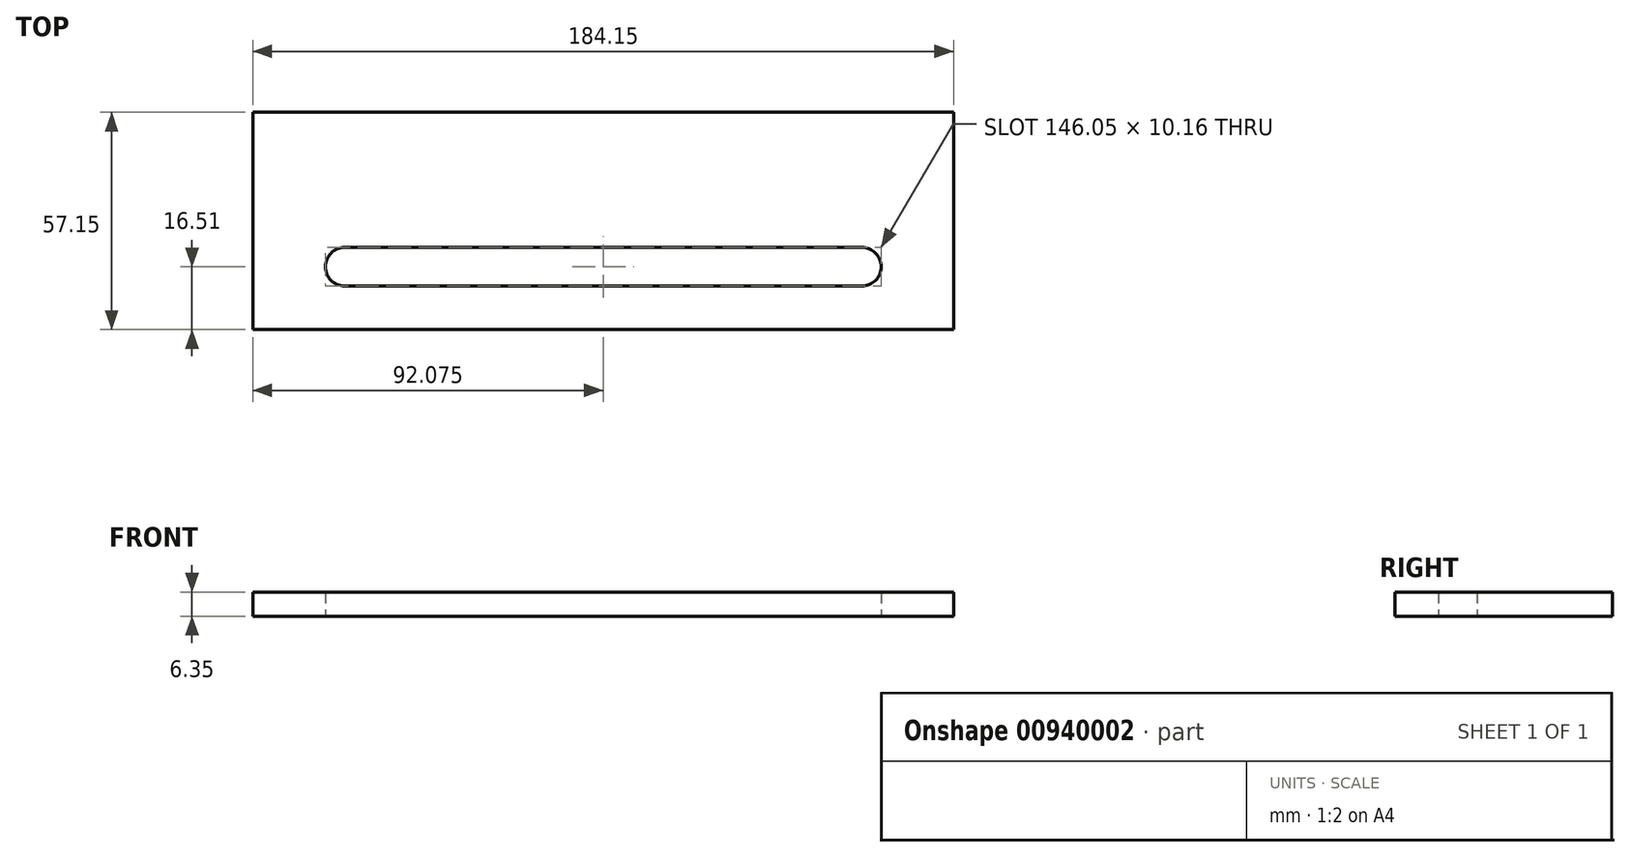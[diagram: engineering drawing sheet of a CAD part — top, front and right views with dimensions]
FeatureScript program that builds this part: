
annotation { "Feature Type Name" : "Feature", "Feature Type Description" : "" }
export const myFeature = defineFeature(function(context is Context, id is Id, definition is map)
    precondition{}
    {
        {
            var Q0;
            Q0=qCreatedBy(makeId("Top.planeOp"),FACE);
            var sketch = newSketch(context, id + "F0", { "sketchPlane" : qUnion([Q0])});
            skLineSegment(sketch, "E0.bottom", {"start": v(0, 0) * mm, "end": v(184.15, 0) * mm});
            skLineSegment(sketch, "E0.top", {"start": v(0, 57.15) * mm, "end": v(184.15, 57.15) * mm});
            skLineSegment(sketch, "E0.left", {"start": v(0, 0) * mm, "end": v(0, 57.15) * mm});
            skLineSegment(sketch, "E0.right", {"start": v(184.15, 0) * mm, "end": v(184.15, 57.15) * mm});
            skLineSegment(sketch, "E1.bottom", {"start": v(24.13, 11.43) * mm, "end": v(160.02, 11.43) * mm});
            skLineSegment(sketch, "E1.top", {"start": v(24.13, 21.59) * mm, "end": v(160.02, 21.59) * mm});
            skLineSegment(sketch, "E1.left", {"start": v(19.05, 16.5) * mm, "end": v(19.05, 16.5) * mm});
            skLineSegment(sketch, "E1.right", {"start": v(165.1, 16.5) * mm, "end": v(165.1, 16.5) * mm});
            skPoint(sketch, "E2.centerSnap0", {"position": v(19.05, 16.5) * mm});
            skPoint(sketch, "E3.visualSharp", {"position": v(19.05, 21.59) * mm});
            skArc(sketch, "E3.filletArc", {"start": v(24.13, 21.59) * mm, "mid": v(20.54, 20.1) * mm, "end": v(19.05, 16.5) * mm});
            skPoint(sketch, "E4.visualSharp", {"position": v(19.05, 11.43) * mm});
            skArc(sketch, "E4.filletArc", {"start": v(19.05, 16.5) * mm, "mid": v(20.54, 12.92) * mm, "end": v(24.13, 11.43) * mm});
            skPoint(sketch, "E5.visualSharp", {"position": v(165.1, 21.59) * mm});
            skArc(sketch, "E5.filletArc", {"start": v(165.1, 16.5) * mm, "mid": v(163.61, 20.1) * mm, "end": v(160.02, 21.59) * mm});
            skPoint(sketch, "E6.visualSharp", {"position": v(165.1, 11.43) * mm});
            skArc(sketch, "E6.filletArc", {"start": v(160.02, 11.43) * mm, "mid": v(163.61, 12.92) * mm, "end": v(165.1, 16.5) * mm});
            skSolve(sketch);
        }
        {
            var Q0;
            Q0=makeQuery(id+"F0.imprint","IMPRINT",FACE,{"disambiguationData":[TD([[makeQuery(id+"F0.imprint","IMPRINT",EDGE,{"derivedFrom":sQuery(id+"F0.wireOp",EDGE,"E0.bottom")}),1.0]])]});
            extrude(context, id + "F1", {"entities" : qUnion([Q0]), "depth" : 6.35 * mm, "offsetDistance" : 25.4 * mm});
        }
    });
